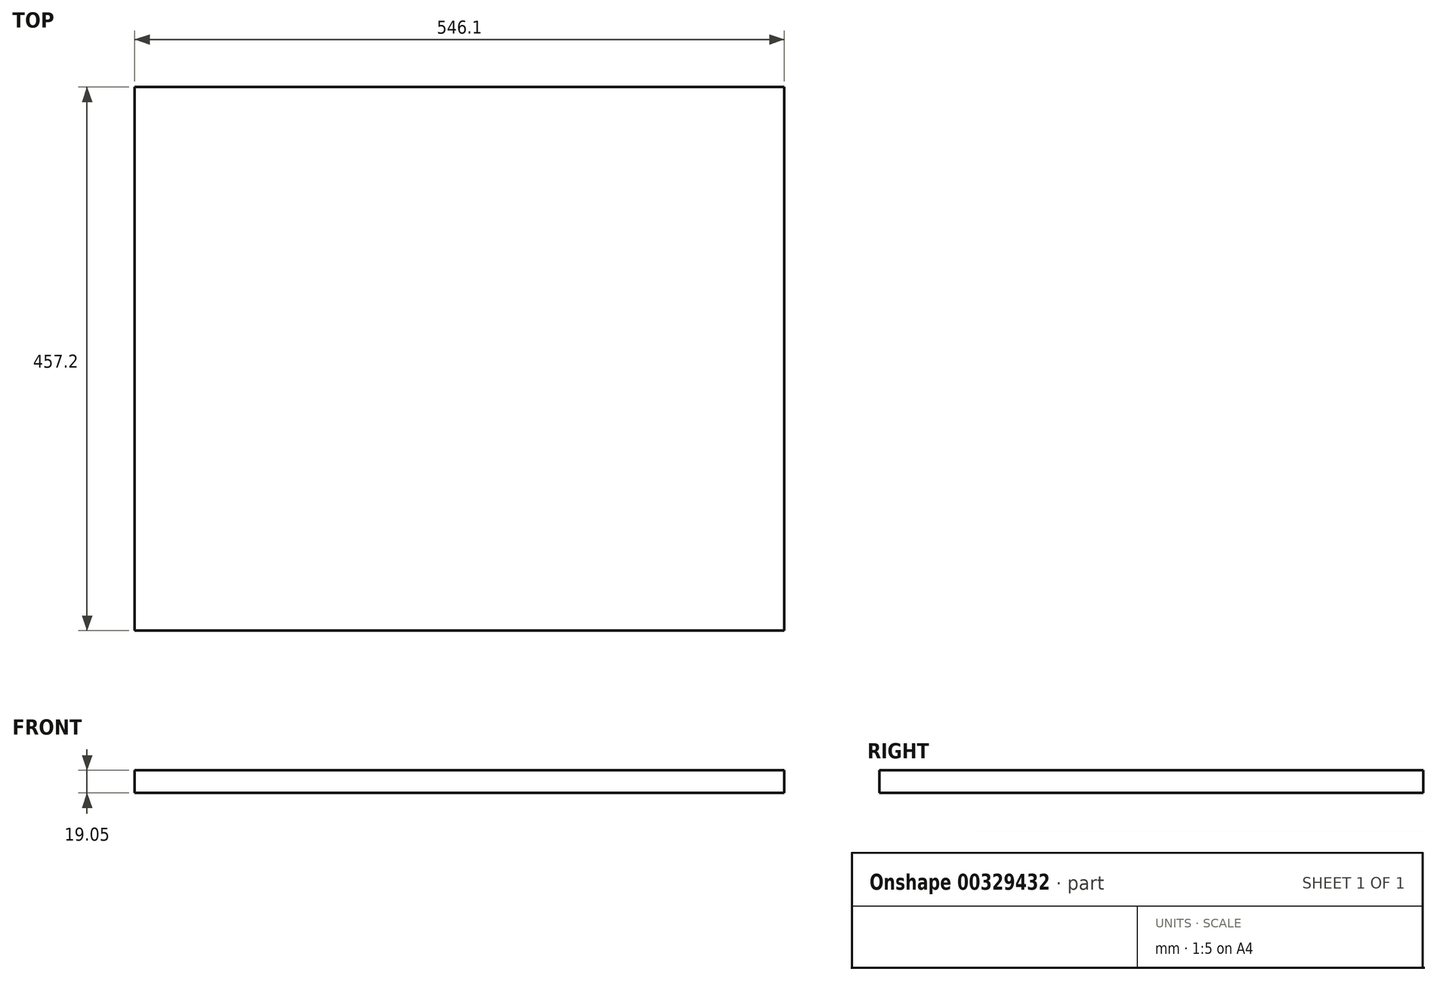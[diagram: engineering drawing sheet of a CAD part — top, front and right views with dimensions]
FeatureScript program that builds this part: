
annotation { "Feature Type Name" : "Feature", "Feature Type Description" : "" }
export const myFeature = defineFeature(function(context is Context, id is Id, definition is map)
    precondition{}
    {
        {
            var Q0;
            Q0=qCreatedBy(makeId("Top.planeOp"),FACE);
            var sketch = newSketch(context, id + "F0", { "sketchPlane" : qUnion([Q0])});
            skLineSegment(sketch, "E0.bottom", {"start": v(273.05, 228.6) * mm, "end": v(-273.05, 228.6) * mm});
            skLineSegment(sketch, "E0.top", {"start": v(273.05, -228.6) * mm, "end": v(-273.05, -228.6) * mm});
            skLineSegment(sketch, "E0.left", {"start": v(273.05, 228.6) * mm, "end": v(273.05, -228.6) * mm});
            skLineSegment(sketch, "E0.right", {"start": v(-273.05, 228.6) * mm, "end": v(-273.05, -228.6) * mm});
            skPoint(sketch, "E0.middle", {"position": v(0, 0) * mm});
            skSolve(sketch);
        }
        {
            var Q0;
            Q0 = qSketchRegion(id + "F0", true);
            extrude(context, id + "F1", {"entities" : qUnion([Q0]), "depth" : 19.05 * mm});
        }
    });
